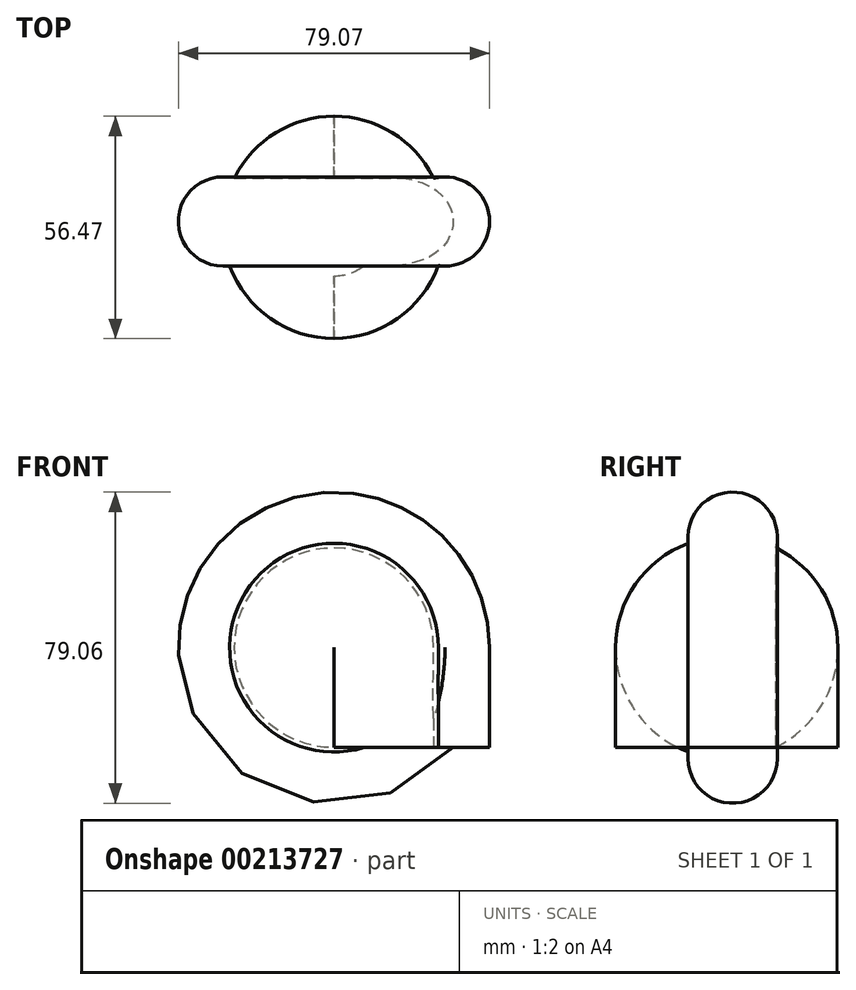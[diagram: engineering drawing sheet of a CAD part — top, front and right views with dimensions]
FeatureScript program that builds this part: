
annotation { "Feature Type Name" : "Feature", "Feature Type Description" : "" }
export const myFeature = defineFeature(function(context is Context, id is Id, definition is map)
    precondition{}
    {
        {
            var Q0;
            Q0=qCreatedBy(makeId("Top.planeOp"),FACE);
            var sketch = newSketch(context, id + "F0", { "sketchPlane" : qUnion([Q0])});
            skArc(sketch, "E0", {"start": v(-31.88, 45.7) * mm, "mid": v(-42.3, 57.2) * mm, "end": v(-57.21, 61.46) * mm});
            skArc(sketch, "E1", {"start": v(-30.7, 23.53) * mm, "mid": v(-17.7, 35.34) * mm, "end": v(-31.88, 45.7) * mm});
            skLineSegment(sketch, "E2", {"start": v(-57.21, 61.46) * mm, "end": v(-57.21, 4.99) * mm});
            skArc(sketch, "E3.trimOffspring", {"start": v(-57.21, 4.99) * mm, "mid": v(-41.03, 10.08) * mm, "end": v(-30.7, 23.53) * mm});
            skSolve(sketch);
        }
        {
            var Q0;
            Q0=makeQuery(id+"F0.imprint","IMPRINT",FACE,{"disambiguationData":[TD([[makeQuery(id+"F0.imprint","IMPRINT",EDGE,{"derivedFrom":sQuery(id+"F0.wireOp",EDGE,"E0")}),1.0]])]});
            extrude(context, id + "F1", {"entities" : qUnion([Q0]), "depth" : 25.4 * mm});
        }
        {
            var Q0;
            Q0=makeQuery(id+"F1.opExtrude","CAP_FACE",FACE,{"disambiguationData":[OSD([sQuery(id+"F0.wireOp",EDGE,"E0"),sQuery(id+"F0.wireOp",EDGE,"E1"),sQuery(id+"F0.wireOp",EDGE,"E2"),sQuery(id+"F0.wireOp",EDGE,"E3.trimOffspring")])],"isStart":false});
            var Q1;
            Q1=makeQuery(id+"F1.opExtrude","CAP_EDGE",EDGE,{"disambiguationData":[OSD([sQuery(id+"F0.wireOp",EDGE,"E2")])],"isStart":false});
            revolve(context, id + "F2", {"operationType" : NewBodyOperationType.ADD, "entities" : qUnion([Q0]), "axis" : qUnion([Q1]), "revolveType" : RevolveType.FULL});
        }
    });
